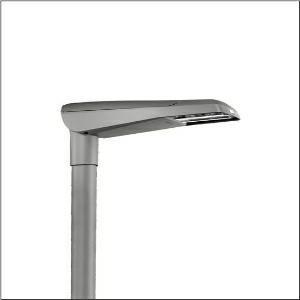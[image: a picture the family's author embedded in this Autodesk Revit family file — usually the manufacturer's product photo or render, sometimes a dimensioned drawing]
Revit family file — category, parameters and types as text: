
# Revit family: streetlight_sl_11_iq_micro___st0_5a_5xc1b51f08ce_ff99
name_source: partatom
category: Lighting Fixtures
units: mm (PartAtom-declared; Revit-internal decimal feet)

## family parameters
Cut with Voids When Loaded = No
Host = Face
Light Source = No
Part Type = Normal
Room Calculation Point = No
Round Connector Dimension = Use Diameter
Shared = No

## types (1)
- --- (1 x LED, 1860 lm, 12.6 W, 3000K)
    Apparent Load = 13 VA
    CIE Flux Codes = 42 72 97 100 100
    Color Rendering = 70
    Color Temperature = 3000K
    Default Elevation = 1800 mm
    Description = Streetlight SL 11 iQ micro, mast luminaire, primary light control with 3 zone facetted reflector, of plastic, silver coated, highly specular, primary optical cover: cover, of PMMA, transparent, light distribution: ST0.5a, light emission: direct distribution, primary light characteristic: asymmetric, installation type: post-top, side-entry, lamps: LED, High Power LED, rated values: 1.860lm | 12,6W | 147,6lm/W (begin service life); end service life: 1.860lm | 12,9W; at 50% lumin. flux: 930lm | 6,8W | 136,8lm/W, colour temperature: 3000K, colour rendering: CRI > 70, light colour: 730, light setting 1 begin service life: 100% | 1.860lm | 12,6W | 147,6lm/W | 3.000K, light setting 1 end service life: 12,9W, further light settings possible, control: Street-Remote, optimised constant luminous flux control (CLO 2.0), Desk-Remote (wireless, voltage-free reading and setting of iQ features in the workshop via application-optimized NFC function/RFID function), Light-Fading, Smart-Wire, Night-Set, Lumen-Switch, Temp-Guard, Auto-Match, with cable H07RN-F 5x 1.5mm², mains connection: 230..240V, AC, 50/60Hz, connection cable pre-assembled, cable length: 5,5m, luminaire housing, of diecast aluminium, powder-coated, Siteco® metallic grey (DB 702S), please order mast flange separately, inclination adjustable without tools: 0°, 5°, 10°, 15° (post-top) | 0°, -5°, -10°, -15° (side-entry), sealing non-destructively replaceable, multi-level sealing system, length: 600mm, width: 174mm, height: 116mm, mast flange for spigot size: 42mm (side-entry): 5XC10008XM4, 60/48mm (side-entry/post-top): 5XC10108XM2, 76/60mm (side-entry/post-top): 5XC10108XM1, equipment: standard, protection rating (complete): IP66, insulation class (complete): insulation class II (safety insulation), certification: CE, ENEC, ENEC+, VDE, impact resistance: IK10, permissible operating ambient temperature for outdoor applications: -25..+50°C, standard-compliant lighting for roads and squares, Environmental Product Declaration (EPD) tested and certified by an independent institute, packaging unit: 1 piece

Light Distribution: ST0.5a
    Height = 116 mm
    Lamp = 1 x LED
    Lamp Light Flux = 1860 lm
    Lamp Power = 12.6 W
    Lamp count = 1
    Length = 600 mm
    Luminous efficacy = 148 lm/W
    Manufacturer = Siteco
    ModVariant = No
    Model = 5XC1B51F08CE
    Number of Poles = 1
    OnlyDefault = Yes
    Power Factor = 1
    Product Name = Streetlight SL 11 iQ micro | ST0.5a
    Product group = mast luminaire | pylon top
    ProductGroupID = 6100
    Protection Class = Protection class II
    Protection Degree = IP 66
    RLX_Detail_Level = 1
    RLX_Emergency_Light_Flux = 0 lm
    RLX_Emergency_Type = 0
    RLX_Emergency_Type_DB = No
    RlxData = <blob elided: 26749 chars, md5=b8784a6e>
    Socket = socket
    Standby Power = 0 W
    System Light Flux = 1860 lm
    System Power = 13 W
    Type Comments = factory setting: luminous flux: 100 % | dim-lin: 254 | 229 mA
    Type Image = l_1006566.jpg
    URL = http://relux.com
    VarID = @adj_020657
    Voltage = 0 V
    Weight = 0.00 kg
    Width = 174 mm

## geometry (parser evidence)
native form markers: Blend x4, Sweep x10
no freeform markers — native parametric forms only
